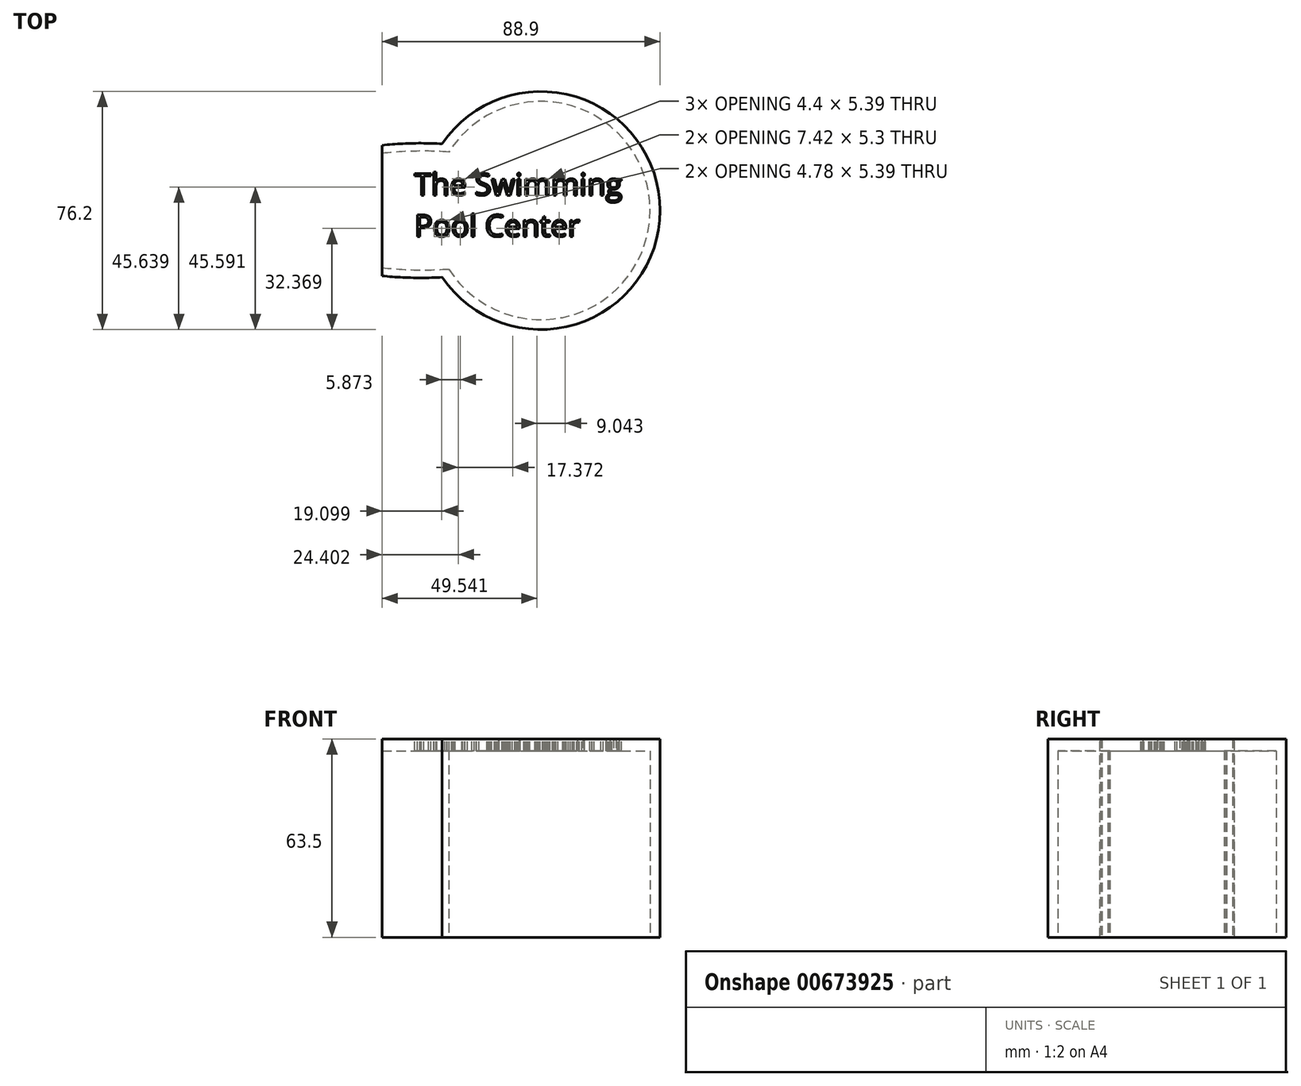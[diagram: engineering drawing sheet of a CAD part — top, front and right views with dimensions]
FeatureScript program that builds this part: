
annotation { "Feature Type Name" : "Feature", "Feature Type Description" : "" }
export const myFeature = defineFeature(function(context is Context, id is Id, definition is map)
    precondition{}
    {
        {
            var Q0;
            Q0=qCreatedBy(makeId("Top.planeOp"),FACE);
            var sketch = newSketch(context, id + "F0", { "sketchPlane" : qUnion([Q0])});
            skCircle(sketch, "E0", {"center": v(0, 0) * mm, "radius": 38.1 * mm});
            skSolve(sketch);
        }
        {
            var Q0;
            Q0=makeQuery(id+"F0.imprint","IMPRINT",FACE,{"disambiguationData":[TD([[makeQuery(id+"F0.imprint","IMPRINT",EDGE,{"derivedFrom":sQuery(id+"F0.wireOp",EDGE,"E0")}),1.0]])]});
            extrude(context, id + "F1", {"entities" : qUnion([Q0]), "depth" : 63.5 * mm, "offsetDistance" : 25 * mm});
        }
        {
            var Q0;
            Q0=qCreatedBy(makeId("Top.planeOp"),FACE);
            var sketch = newSketch(context, id + "F2", { "sketchPlane" : qUnion([Q0])});
            skEllipse(sketch, "E1", {"center": v(-38.48, 0) * mm, "majorRadius": 50.8 * mm, "minorRadius": 21.54 * mm, "majorAxis": v(-1, 0)});
            skSolve(sketch);
        }
        {
            var Q0;
            Q0=makeQuery(id+"F2.imprint","IMPRINT",FACE,{"disambiguationData":[TD([[makeQuery(id+"F2.imprint","IMPRINT",EDGE,{"derivedFrom":sQuery(id+"F2.wireOp",EDGE,"E1")}),1.0]])]});
            extrude(context, id + "F3", {"entities" : qUnion([Q0]), "operationType" : NewBodyOperationType.ADD, "depth" : 63.5 * mm, "offsetDistance" : 25 * mm});
        }
        {
            var Q0;
            Q0=qCreatedBy(makeId("Top.planeOp"),FACE);
            var sketch = newSketch(context, id + "F4", { "sketchPlane" : qUnion([Q0])});
            skLineSegment(sketch, "E2.bottom", {"start": v(-93.45, 23.37) * mm, "end": v(-50.8, 23.37) * mm});
            skLineSegment(sketch, "E2.top", {"start": v(-93.45, -22.58) * mm, "end": v(-50.8, -22.58) * mm});
            skLineSegment(sketch, "E2.left", {"start": v(-93.45, 23.37) * mm, "end": v(-93.45, -22.58) * mm});
            skLineSegment(sketch, "E2.right", {"start": v(-50.8, 23.37) * mm, "end": v(-50.8, -22.58) * mm});
            skSolve(sketch);
        }
        {
            var Q0;
            Q0=makeQuery(id+"F4.imprint","IMPRINT",FACE,{"disambiguationData":[TD([[makeQuery(id+"F4.imprint","IMPRINT",EDGE,{"derivedFrom":sQuery(id+"F4.wireOp",EDGE,"E2.bottom")}),-1.0]])]});
            var Q1;
            Q1=sQuery(id+"F4.wireOp",EDGE,"E2.bottom");
            var Q2;
            Q2=sQuery(id+"F4.wireOp",EDGE,"E2.left");
            var Q3;
            Q3=sQuery(id+"F4.wireOp",EDGE,"E2.top");
            var Q4;
            Q4=sQuery(id+"F4.wireOp",EDGE,"E2.right");
            extrude(context, id + "F5", {"entities" : qUnion([Q0]), "operationType" : NewBodyOperationType.REMOVE, "surfaceEntities" : qUnion([Q1, Q2, Q3, Q4]), "depth" : 38.1 * mm, "offsetDistance" : 25 * mm});
        }
        {
            var Q0;
            Q0=qCreatedBy(makeId("Top.planeOp"),FACE);
            var sketch = newSketch(context, id + "F6", { "sketchPlane" : qUnion([Q0])});
            skCircle(sketch, "E3", {"center": v(0, 0) * mm, "radius": 34.93 * mm});
            skEllipse(sketch, "E4", {"center": v(-37.76, 0) * mm, "majorRadius": 47.73 * mm, "minorRadius": 19.02 * mm, "majorAxis": v(-1, 0)});
            skSolve(sketch);
        }
        {
            var Q0;
            {var subQ0=sQuery(id+"F6.wireOp",EDGE,"E4");var subQ1=sQuery(id+"F6.wireOp",EDGE,"E3");var subQ2=makeQuery(id+"F6.imprint","INTERSECT",VERTEX,{"disambiguationData":[OD(0.0)],"derivedFrom":[subQ1,subQ0]});Q0=makeQuery(id+"F6.imprint","IMPRINT",FACE,{"disambiguationData":[TD([[makeQuery(id+"F6.imprint","IMPRINT",EDGE,{"disambiguationData":[TD([[subQ2,1.0]])],"derivedFrom":subQ1}),-1.0]])]});}
            var Q1;
            {var subQ0=sQuery(id+"F6.wireOp",EDGE,"E4");var subQ1=sQuery(id+"F6.wireOp",EDGE,"E3");var subQ2=makeQuery(id+"F6.imprint","INTERSECT",VERTEX,{"disambiguationData":[OD(0.0)],"derivedFrom":[subQ1,subQ0]});Q1=makeQuery(id+"F6.imprint","IMPRINT",FACE,{"disambiguationData":[TD([[makeQuery(id+"F6.imprint","IMPRINT",EDGE,{"disambiguationData":[TD([[subQ2,1.0]])],"derivedFrom":subQ1}),1.0]])]});}
            var Q2;
            {var subQ0=sQuery(id+"F6.wireOp",EDGE,"E4");var subQ1=sQuery(id+"F6.wireOp",EDGE,"E3");var subQ2=makeQuery(id+"F6.imprint","INTERSECT",VERTEX,{"disambiguationData":[OD(0.0)],"derivedFrom":[subQ1,subQ0]});Q2=makeQuery(id+"F6.imprint","IMPRINT",FACE,{"disambiguationData":[TD([[makeQuery(id+"F6.imprint","IMPRINT",EDGE,{"disambiguationData":[TD([[subQ2,-1.0]])],"derivedFrom":subQ1}),1.0]])]});}
            extrude(context, id + "F7", {"entities" : qUnion([Q0, Q1, Q2]), "operationType" : NewBodyOperationType.REMOVE, "depth" : 59.7 * mm, "offsetDistance" : 25 * mm});
        }
        {
            var Q0;
            Q0=makeQuery(id+"F3.boolean.opBoolean","MERGE",FACE,{"derivedFrom":[makeQuery(id+"F1.opExtrude","CAP_FACE",FACE,{"disambiguationData":[OSD([sQuery(id+"F0.wireOp",EDGE,"E0")])],"isStart":false}),makeQuery(id+"F3.opExtrude","CAP_FACE",FACE,{"disambiguationData":[OSD([sQuery(id+"F2.wireOp",EDGE,"E1")])],"isStart":false})]});
            var sketch = newSketch(context, id + "F8", { "sketchPlane" : qUnion([Q0])});
            skText(sketch, "E5", { "text": "The Swimming \nPool Center\n", "fontName": "OpenSans-Regular.ttf"});
            const initialGuessF8  = {"E5": [-0.04049, 0.00489, 1, 0, 0.007]};
            skSetInitialGuess(sketch, initialGuessF8);
            skSolve(sketch);
        }
        {
            var Q0;
            Q0 = qSketchRegion(id + "F4", true);
            extrude(context, id + "F9", {"entities" : qUnion([Q0]), "operationType" : NewBodyOperationType.REMOVE, "depth" : 126 * mm, "offsetDistance" : 25 * mm});
        }
        {
            var Q0;
            Q0 = qSketchRegion(id + "F8", true);
            extrude(context, id + "F10", {"entities" : qUnion([Q0]), "operationType" : NewBodyOperationType.REMOVE, "oppositeDirection" : true, "depth" : 25 * mm, "offsetDistance" : 25 * mm});
        }
    });
